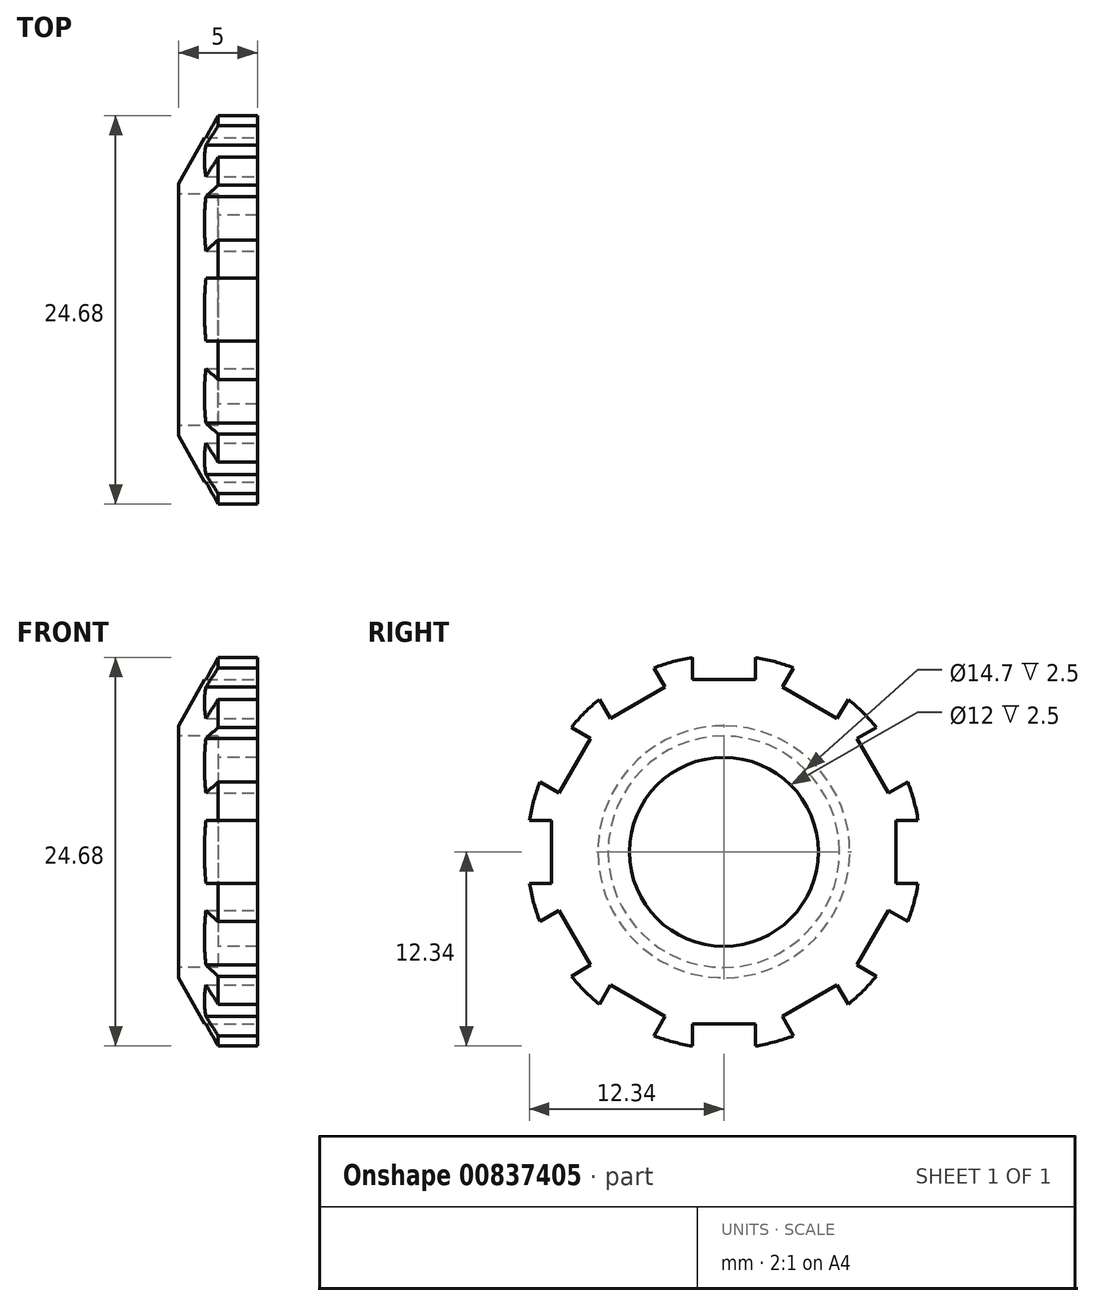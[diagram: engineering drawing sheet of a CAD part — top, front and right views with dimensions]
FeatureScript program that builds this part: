
annotation { "Feature Type Name" : "Feature", "Feature Type Description" : "" }
export const myFeature = defineFeature(function(context is Context, id is Id, definition is map)
    precondition{}
    {
        {
            var Q0;
            Q0=qCreatedBy(makeId("Front.planeOp"),FACE);
            var sketch = newSketch(context, id + "F0", { "sketchPlane" : qUnion([Q0])});
            skLineSegment(sketch, "E0", {"start": v(0, 8) * mm, "end": v(2.5, 12.5) * mm});
            skLineSegment(sketch, "E1", {"start": v(2.5, 12.5) * mm, "end": v(5, 12.5) * mm});
            skLineSegment(sketch, "E2", {"start": v(5, 12.5) * mm, "end": v(5, 6) * mm});
            skLineSegment(sketch, "E3", {"start": v(2.5, 6) * mm, "end": v(5, 6) * mm});
            skPoint(sketch, "E4.orphan", {"position": v(5, 0) * mm});
            skLineSegment(sketch, "E5", {"start": v(0, 7.35) * mm, "end": v(2.5, 7.35) * mm});
            skLineSegment(sketch, "E6", {"start": v(2.5, 7.35) * mm, "end": v(2.5, 6) * mm});
            skLineSegment(sketch, "E7", {"start": v(0, 7.35) * mm, "end": v(0, 8) * mm});
            skLineSegment(sketch, "E8", {"start": v(0, 0) * mm, "end": v(5, 0) * mm});
            skSolve(sketch);
        }
        {
            var Q0;
            Q0 = qSketchRegion(id + "F0", true);
            var Q1;
            Q1=sQuery(id+"F0.wireOp",EDGE,"E8");
            revolve(context, id + "F1", {"surfaceOperationType" : NewSurfaceOperationType.NEW, "entities" : qUnion([Q0]), "axis" : qUnion([Q1]), "revolveType" : RevolveType.FULL});
        }
        {
            var Q0;
            Q0=makeQuery(id+"F1.opRevolve","SWEPT_FACE",FACE,{"disambiguationData":[OSD([sQuery(id+"F0.wireOp",EDGE,"E2")])]});
            var sketch = newSketch(context, id + "F2", { "sketchPlane" : qUnion([Q0])});
            skLineSegment(sketch, "E9", {"start": v(0, 12.5) * mm, "end": v(0, 10.93) * mm});
            skLineSegment(sketch, "E10", {"start": v(0, 10.93) * mm, "end": v(-2, 10.93) * mm});
            skLineSegment(sketch, "E11", {"start": v(-2, 10.93) * mm, "end": v(-2, 14.15) * mm});
            skLineSegment(sketch, "E12", {"start": v(-2, 14.15) * mm, "end": v(2, 14.15) * mm});
            skLineSegment(sketch, "E13", {"start": v(2, 14.15) * mm, "end": v(2, 10.93) * mm});
            skLineSegment(sketch, "E14", {"start": v(2, 10.93) * mm, "end": v(0, 10.93) * mm});
            skLineSegment(sketch, "E15.1.0", {"start": v(-7.2, 8.47) * mm, "end": v(-8.8, 11.26) * mm});
            skLineSegment(sketch, "E15.1.1", {"start": v(-8.8, 11.26) * mm, "end": v(-5.34, 13.26) * mm});
            skLineSegment(sketch, "E15.1.2", {"start": v(-5.34, 13.26) * mm, "end": v(-3.74, 10.47) * mm});
            skLineSegment(sketch, "E15.1.3", {"start": v(-3.74, 10.47) * mm, "end": v(-5.47, 9.47) * mm});
            skLineSegment(sketch, "E15.1.4", {"start": v(-5.47, 9.47) * mm, "end": v(-7.2, 8.47) * mm});
            skLineSegment(sketch, "E15.2.0", {"start": v(-10.47, 3.74) * mm, "end": v(-13.26, 5.34) * mm});
            skLineSegment(sketch, "E15.2.1", {"start": v(-13.26, 5.34) * mm, "end": v(-11.26, 8.8) * mm});
            skLineSegment(sketch, "E15.2.2", {"start": v(-11.26, 8.8) * mm, "end": v(-8.47, 7.2) * mm});
            skLineSegment(sketch, "E15.2.3", {"start": v(-8.47, 7.2) * mm, "end": v(-9.47, 5.47) * mm});
            skLineSegment(sketch, "E15.2.4", {"start": v(-9.47, 5.47) * mm, "end": v(-10.47, 3.74) * mm});
            skLineSegment(sketch, "E15.3.0", {"start": v(-10.93, -2) * mm, "end": v(-14.15, -2) * mm});
            skLineSegment(sketch, "E15.3.1", {"start": v(-14.15, -2) * mm, "end": v(-14.15, 2) * mm});
            skLineSegment(sketch, "E15.3.2", {"start": v(-14.15, 2) * mm, "end": v(-10.93, 2) * mm});
            skLineSegment(sketch, "E15.3.3", {"start": v(-10.93, 2) * mm, "end": v(-10.93, 0) * mm});
            skLineSegment(sketch, "E15.3.4", {"start": v(-10.93, 0) * mm, "end": v(-10.93, -2) * mm});
            skLineSegment(sketch, "E15.4.0", {"start": v(-8.47, -7.2) * mm, "end": v(-11.26, -8.8) * mm});
            skLineSegment(sketch, "E15.4.1", {"start": v(-11.26, -8.8) * mm, "end": v(-13.26, -5.34) * mm});
            skLineSegment(sketch, "E15.4.2", {"start": v(-13.26, -5.34) * mm, "end": v(-10.47, -3.74) * mm});
            skLineSegment(sketch, "E15.4.3", {"start": v(-10.47, -3.74) * mm, "end": v(-9.47, -5.47) * mm});
            skLineSegment(sketch, "E15.4.4", {"start": v(-9.47, -5.47) * mm, "end": v(-8.47, -7.2) * mm});
            skLineSegment(sketch, "E15.5.0", {"start": v(-3.74, -10.47) * mm, "end": v(-5.34, -13.26) * mm});
            skLineSegment(sketch, "E15.5.1", {"start": v(-5.34, -13.26) * mm, "end": v(-8.8, -11.26) * mm});
            skLineSegment(sketch, "E15.5.2", {"start": v(-8.8, -11.26) * mm, "end": v(-7.2, -8.47) * mm});
            skLineSegment(sketch, "E15.5.3", {"start": v(-7.2, -8.47) * mm, "end": v(-5.47, -9.47) * mm});
            skLineSegment(sketch, "E15.5.4", {"start": v(-5.47, -9.47) * mm, "end": v(-3.74, -10.47) * mm});
            skLineSegment(sketch, "E15.6.0", {"start": v(2, -10.93) * mm, "end": v(2, -14.15) * mm});
            skLineSegment(sketch, "E15.6.1", {"start": v(2, -14.15) * mm, "end": v(-2, -14.15) * mm});
            skLineSegment(sketch, "E15.6.2", {"start": v(-2, -14.15) * mm, "end": v(-2, -10.93) * mm});
            skLineSegment(sketch, "E15.6.3", {"start": v(-2, -10.93) * mm, "end": v(0, -10.93) * mm});
            skLineSegment(sketch, "E15.6.4", {"start": v(0, -10.93) * mm, "end": v(2, -10.93) * mm});
            skLineSegment(sketch, "E15.7.0", {"start": v(7.2, -8.47) * mm, "end": v(8.8, -11.26) * mm});
            skLineSegment(sketch, "E15.7.1", {"start": v(8.8, -11.26) * mm, "end": v(5.34, -13.26) * mm});
            skLineSegment(sketch, "E15.7.2", {"start": v(5.34, -13.26) * mm, "end": v(3.74, -10.47) * mm});
            skLineSegment(sketch, "E15.7.3", {"start": v(3.74, -10.47) * mm, "end": v(5.47, -9.47) * mm});
            skLineSegment(sketch, "E15.7.4", {"start": v(5.47, -9.47) * mm, "end": v(7.2, -8.47) * mm});
            skLineSegment(sketch, "E15.8.0", {"start": v(10.47, -3.74) * mm, "end": v(13.26, -5.34) * mm});
            skLineSegment(sketch, "E15.8.1", {"start": v(13.26, -5.34) * mm, "end": v(11.26, -8.8) * mm});
            skLineSegment(sketch, "E15.8.2", {"start": v(11.26, -8.8) * mm, "end": v(8.47, -7.2) * mm});
            skLineSegment(sketch, "E15.8.3", {"start": v(8.47, -7.2) * mm, "end": v(9.47, -5.47) * mm});
            skLineSegment(sketch, "E15.8.4", {"start": v(9.47, -5.47) * mm, "end": v(10.47, -3.74) * mm});
            skLineSegment(sketch, "E15.9.0", {"start": v(10.93, 2) * mm, "end": v(14.15, 2) * mm});
            skLineSegment(sketch, "E15.9.1", {"start": v(14.15, 2) * mm, "end": v(14.15, -2) * mm});
            skLineSegment(sketch, "E15.9.2", {"start": v(14.15, -2) * mm, "end": v(10.93, -2) * mm});
            skLineSegment(sketch, "E15.9.3", {"start": v(10.93, -2) * mm, "end": v(10.93, 0) * mm});
            skLineSegment(sketch, "E15.9.4", {"start": v(10.93, 0) * mm, "end": v(10.93, 2) * mm});
            skLineSegment(sketch, "E15.10.0", {"start": v(8.47, 7.2) * mm, "end": v(11.26, 8.8) * mm});
            skLineSegment(sketch, "E15.10.1", {"start": v(11.26, 8.8) * mm, "end": v(13.26, 5.34) * mm});
            skLineSegment(sketch, "E15.10.2", {"start": v(13.26, 5.34) * mm, "end": v(10.47, 3.74) * mm});
            skLineSegment(sketch, "E15.10.3", {"start": v(10.47, 3.74) * mm, "end": v(9.47, 5.47) * mm});
            skLineSegment(sketch, "E15.10.4", {"start": v(9.47, 5.47) * mm, "end": v(8.47, 7.2) * mm});
            skLineSegment(sketch, "E15.11.0", {"start": v(3.74, 10.47) * mm, "end": v(5.34, 13.26) * mm});
            skLineSegment(sketch, "E15.11.1", {"start": v(5.34, 13.26) * mm, "end": v(8.8, 11.26) * mm});
            skLineSegment(sketch, "E15.11.2", {"start": v(8.8, 11.26) * mm, "end": v(7.2, 8.47) * mm});
            skLineSegment(sketch, "E15.11.3", {"start": v(7.2, 8.47) * mm, "end": v(5.47, 9.47) * mm});
            skLineSegment(sketch, "E15.11.4", {"start": v(5.47, 9.47) * mm, "end": v(3.74, 10.47) * mm});
            skPoint(sketch, "E15.center", {"position": v(0, 0) * mm});
            skSolve(sketch);
        }
        {
            var Q0;
            Q0 = qSketchRegion(id + "F2", true);
            extrude(context, id + "F3", {"entities" : qUnion([Q0]), "operationType" : NewBodyOperationType.REMOVE, "oppositeDirection" : true, "depth" : 25 * mm, "offsetDistance" : 25 * mm});
        }
    });
